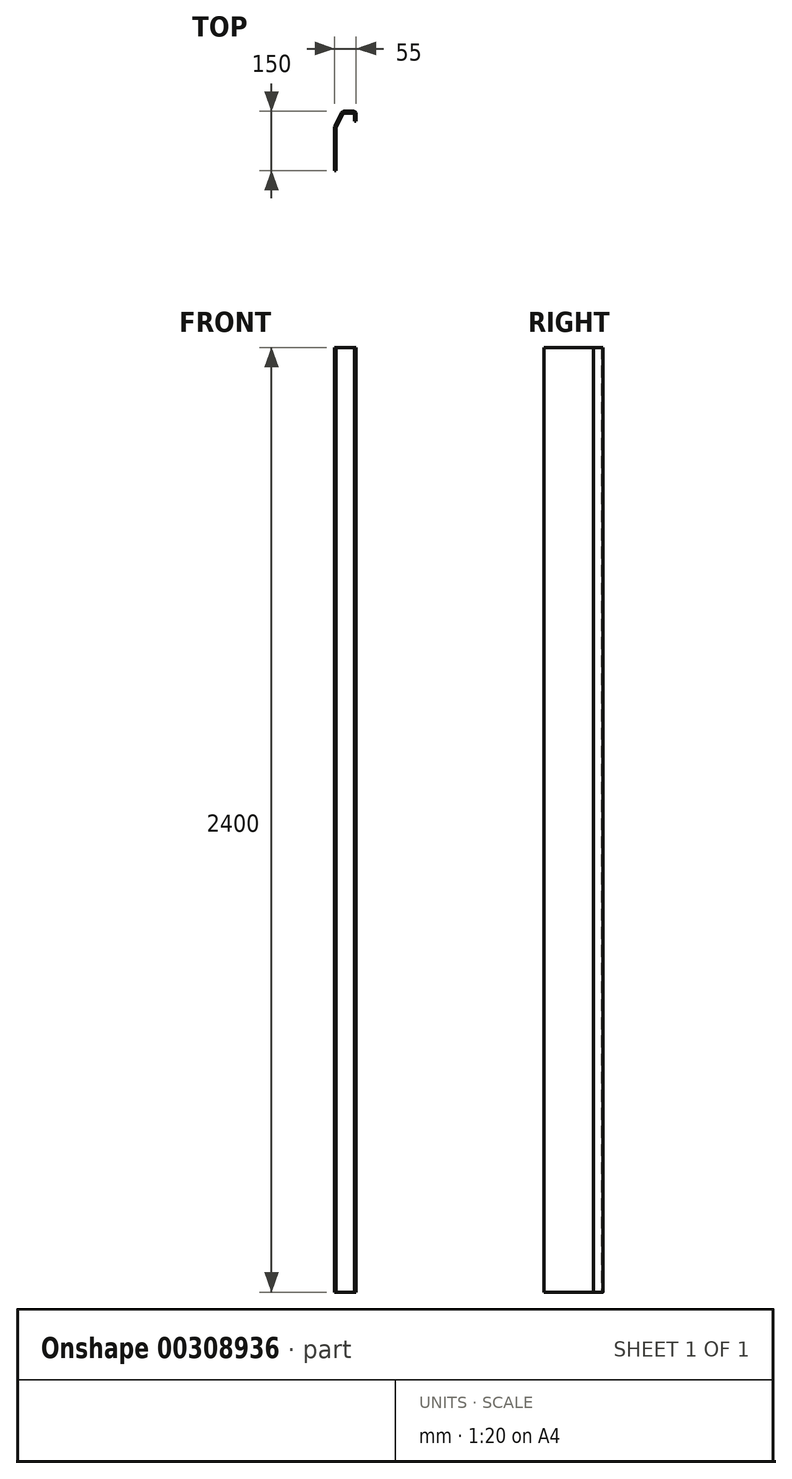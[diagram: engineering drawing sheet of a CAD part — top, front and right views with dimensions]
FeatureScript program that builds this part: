
annotation { "Feature Type Name" : "Feature", "Feature Type Description" : "" }
export const myFeature = defineFeature(function(context is Context, id is Id, definition is map)
    precondition{}
    {
        {
            var Q0;
            Q0=qCreatedBy(makeId("Top.planeOp"),FACE);
            var sketch = newSketch(context, id + "F0", { "sketchPlane" : qUnion([Q0])});
            skLineSegment(sketch, "E0", {"start": v(0, 0) * mm, "end": v(-4, 0) * mm});
            skLineSegment(sketch, "E1", {"start": v(-4, 0) * mm, "end": v(-4, 150) * mm, "construction": true});
            skLineSegment(sketch, "E2", {"start": v(-4, 150) * mm, "end": v(51, 150) * mm, "construction": true});
            skLineSegment(sketch, "E3", {"start": v(51, 144) * mm, "end": v(51, 125) * mm});
            skLineSegment(sketch, "E4", {"start": v(-4, 0) * mm, "end": v(-4, 109.31) * mm});
            skLineSegment(sketch, "E5", {"start": v(-3.36, 112) * mm, "end": v(14.1, 146.7) * mm});
            skLineSegment(sketch, "E6", {"start": v(19.46, 150) * mm, "end": v(45, 150) * mm});
            skLineSegment(sketch, "E7.0", {"start": v(47, 140) * mm, "end": v(47, 125) * mm});
            skLineSegment(sketch, "E7.1", {"start": v(21.92, 146) * mm, "end": v(41, 146) * mm});
            skLineSegment(sketch, "E7.2", {"start": v(0.64, 111.06) * mm, "end": v(16.56, 142.7) * mm});
            skLineSegment(sketch, "E7.3", {"start": v(0, 0) * mm, "end": v(0, 108.36) * mm});
            skLineSegment(sketch, "E8", {"start": v(47, 125) * mm, "end": v(51, 125) * mm});
            skPoint(sketch, "E9.visualSharp", {"position": v(-4, 110.74) * mm});
            skArc(sketch, "E9.filletArc", {"start": v(-3.36, 112) * mm, "mid": v(-3.84, 110.7) * mm, "end": v(-4, 109.31) * mm});
            skPoint(sketch, "E10.visualSharp", {"position": v(18.23, 146) * mm});
            skArc(sketch, "E10.filletArc", {"start": v(21.92, 146) * mm, "mid": v(18.78, 145.1) * mm, "end": v(16.56, 142.7) * mm});
            skPoint(sketch, "E11.visualSharp", {"position": v(15.76, 150) * mm});
            skArc(sketch, "E11.filletArc", {"start": v(19.46, 150) * mm, "mid": v(16.31, 149.1) * mm, "end": v(14.1, 146.7) * mm});
            skPoint(sketch, "E12.visualSharp", {"position": v(0, 109.79) * mm});
            skArc(sketch, "E12.filletArc", {"start": v(0.64, 111.06) * mm, "mid": v(0.16, 109.75) * mm, "end": v(0, 108.36) * mm});
            skPoint(sketch, "E13.visualSharp", {"position": v(47, 146) * mm});
            skArc(sketch, "E13.filletArc", {"start": v(47, 140) * mm, "mid": v(45.24, 144.24) * mm, "end": v(41, 146) * mm});
            skPoint(sketch, "E14.visualSharp", {"position": v(51, 150) * mm});
            skArc(sketch, "E14.filletArc", {"start": v(51, 144) * mm, "mid": v(49.24, 148.24) * mm, "end": v(45, 150) * mm});
            skSolve(sketch);
        }
        {
            var Q0;
            Q0 = qSketchRegion(id + "F0", true);
            extrude(context, id + "F1", {"entities" : qUnion([Q0]), "depth" : 2400 * mm});
        }
    });
